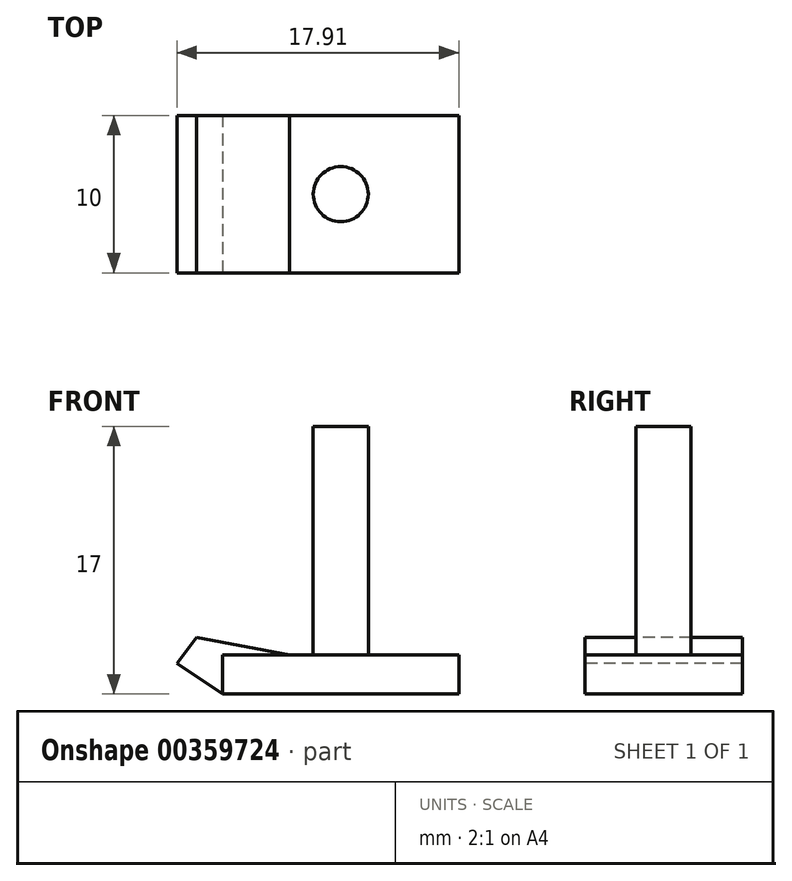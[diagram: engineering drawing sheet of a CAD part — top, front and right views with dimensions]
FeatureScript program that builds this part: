
annotation { "Feature Type Name" : "Feature", "Feature Type Description" : "" }
export const myFeature = defineFeature(function(context is Context, id is Id, definition is map)
    precondition{}
    {
        {
            var Q0;
            Q0=qCreatedBy(makeId("Top.planeOp"),FACE);
            var sketch = newSketch(context, id + "F0", { "sketchPlane" : qUnion([Q0])});
            skLineSegment(sketch, "E0.bottom", {"start": v(7.5, 5) * mm, "end": v(-7.5, 5) * mm});
            skLineSegment(sketch, "E0.top", {"start": v(7.5, -5) * mm, "end": v(-7.5, -5) * mm});
            skLineSegment(sketch, "E0.left", {"start": v(7.5, 5) * mm, "end": v(7.5, -5) * mm});
            skLineSegment(sketch, "E0.right", {"start": v(-7.5, 5) * mm, "end": v(-7.5, -5) * mm});
            skPoint(sketch, "E0.middle", {"position": v(0, 0) * mm});
            skCircle(sketch, "E1", {"center": v(0, 0) * mm, "radius": 1.75 * mm});
            skSolve(sketch);
        }
        {
            var Q0;
            Q0=makeQuery(id+"F0.imprint","IMPRINT",FACE,{"disambiguationData":[TD([[makeQuery(id+"F0.imprint","IMPRINT",EDGE,{"derivedFrom":sQuery(id+"F0.wireOp",EDGE,"E1")}),1.0]])]});
            extrude(context, id + "F1", {"entities" : qUnion([Q0]), "depth" : 17 * mm});
        }
        {
            var Q0;
            Q0=makeQuery(id+"F0.imprint","IMPRINT",FACE,{"disambiguationData":[TD([[makeQuery(id+"F0.imprint","IMPRINT",EDGE,{"derivedFrom":sQuery(id+"F0.wireOp",EDGE,"E0.bottom")}),1.0]])]});
            extrude(context, id + "F2", {"entities" : qUnion([Q0]), "operationType" : NewBodyOperationType.ADD, "depth" : 2.5 * mm});
        }
        {
            var Q0;
            Q0=makeQuery(id+"F2.opExtrude","SWEPT_FACE",FACE,{"disambiguationData":[OSD([sQuery(id+"F0.wireOp",EDGE,"E0.top")])]});
            var sketch = newSketch(context, id + "F3", { "sketchPlane" : qUnion([Q0])});
            skLineSegment(sketch, "E2", {"start": v(-7.5, 0) * mm, "end": v(-10.41, 1.94) * mm});
            skLineSegment(sketch, "E3", {"start": v(-7.5, 2.5) * mm, "end": v(-9.16, 3.6) * mm});
            skLineSegment(sketch, "E4", {"start": v(-9.16, 3.6) * mm, "end": v(-10.41, 1.94) * mm});
            skLineSegment(sketch, "E5", {"start": v(-9.16, 3.6) * mm, "end": v(-3.27, 2.5) * mm});
            skSolve(sketch);
        }
        {
            var Q0;
            Q0=makeQuery(id+"F3.imprint","IMPRINT",FACE,{"disambiguationData":[TD([[makeQuery(id+"F3.imprint","IMPRINT",EDGE,{"derivedFrom":sQuery(id+"F3.wireOp",EDGE,"E2")}),-1.0]])]});
            var Q1;
            {var subQ0=sQuery(id+"F3.wireOp",EDGE,"E3");Q1=makeQuery(id+"F3.imprint","IMPRINT",FACE,{"disambiguationData":[TD([[makeQuery(id+"F3.imprint","IMPRINT",EDGE,{"derivedFrom":subQ0}),-1.0]])]});}
            extrude(context, id + "F4", {"entities" : qUnion([Q0, Q1]), "oppositeDirection" : true, "depth" : 10 * mm});
        }
    });
